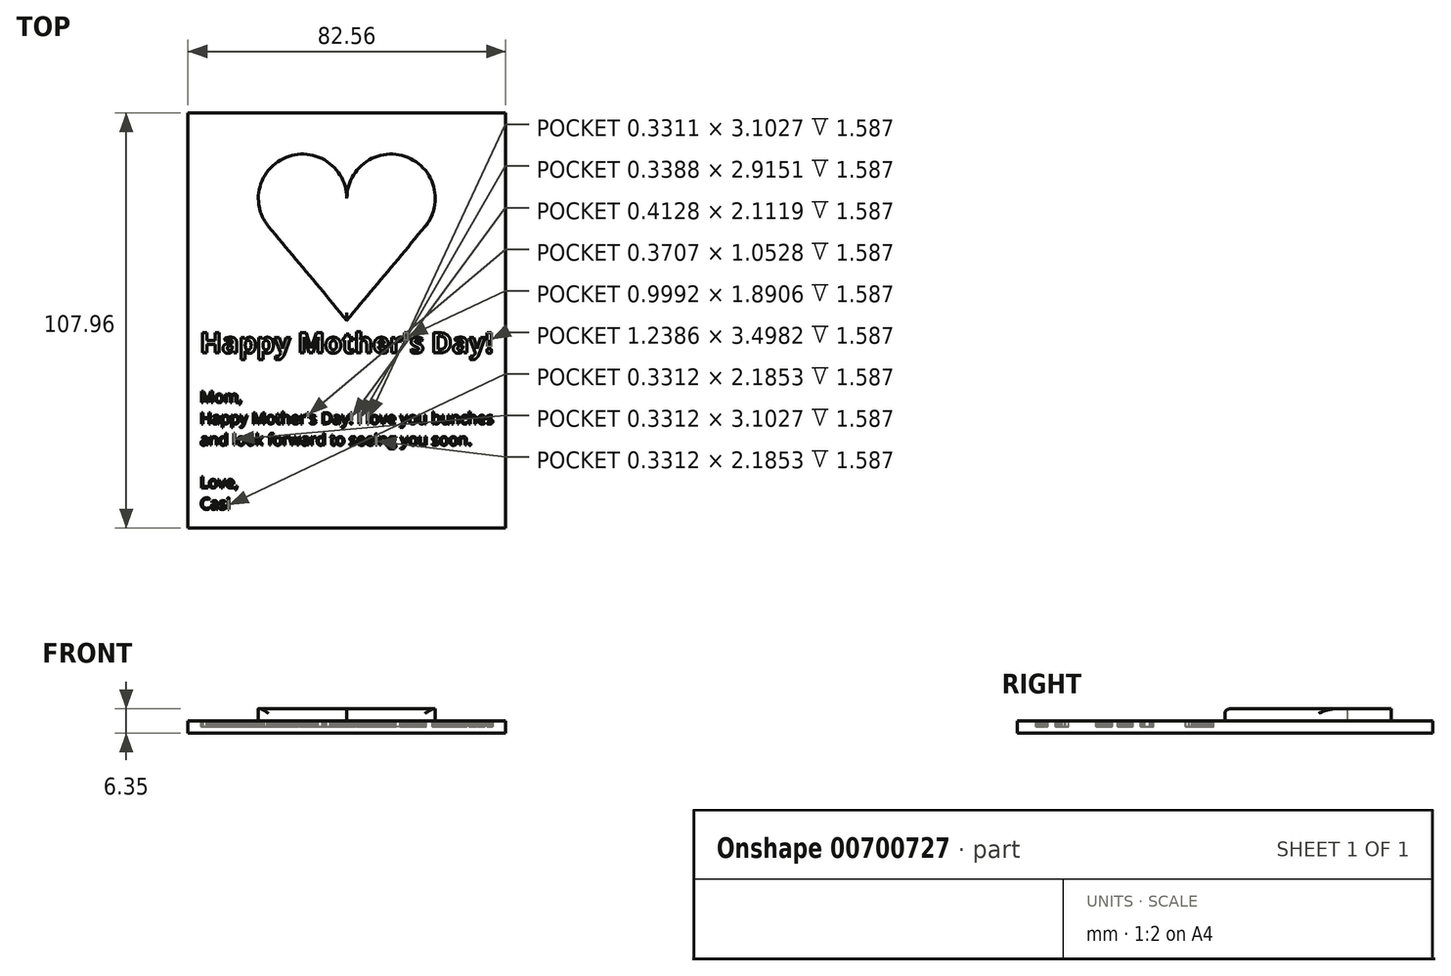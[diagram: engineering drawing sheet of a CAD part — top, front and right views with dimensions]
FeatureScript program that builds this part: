
annotation { "Feature Type Name" : "Feature", "Feature Type Description" : "" }
export const myFeature = defineFeature(function(context is Context, id is Id, definition is map)
    precondition{}
    {
        {
            var Q0;
            Q0=qCreatedBy(makeId("Top.planeOp"),FACE);
            var sketch = newSketch(context, id + "F0", { "sketchPlane" : qUnion([Q0])});
            skLineSegment(sketch, "E0.bottom", {"start": v(41.28, -53.98) * mm, "end": v(-41.28, -53.98) * mm});
            skLineSegment(sketch, "E0.top", {"start": v(41.28, 53.97) * mm, "end": v(-41.28, 53.97) * mm});
            skLineSegment(sketch, "E0.left", {"start": v(41.28, -53.98) * mm, "end": v(41.28, 53.97) * mm});
            skLineSegment(sketch, "E0.right", {"start": v(-41.28, -53.98) * mm, "end": v(-41.28, 53.97) * mm});
            skPoint(sketch, "E0.middle", {"position": v(0, 0) * mm});
            skSolve(sketch);
        }
        {
            var Q0;
            Q0 = qSketchRegion(id + "F0", true);
            extrude(context, id + "F1", {"entities" : qUnion([Q0]), "depth" : 3.17 * mm, "offsetDistance" : 25.4 * mm});
        }
        {
            var Q0;
            Q0=makeQuery(id+"F1.opExtrude","CAP_FACE",FACE,{"disambiguationData":[OSD([sQuery(id+"F0.wireOp",EDGE,"E0.bottom"),sQuery(id+"F0.wireOp",EDGE,"E0.top"),sQuery(id+"F0.wireOp",EDGE,"E0.left"),sQuery(id+"F0.wireOp",EDGE,"E0.right")])],"isStart":false});
            var sketch = newSketch(context, id + "F2", { "sketchPlane" : qUnion([Q0])});
            skLineSegment(sketch, "E1", {"start": v(0, 0) * mm, "end": v(-20.32, 24.4) * mm});
            skArc(sketch, "E2", {"start": v(-20.32, 24.4) * mm, "mid": v(-15.4, 42.55) * mm, "end": v(0, 31.75) * mm});
            skArc(sketch, "E3.MirrorCS", {"start": v(20.32, 24.4) * mm, "mid": v(15.4, 42.55) * mm, "end": v(0, 31.75) * mm});
            skLineSegment(sketch, "E4.MirrorCS", {"start": v(0, 0) * mm, "end": v(20.32, 24.4) * mm});
            skSolve(sketch);
        }
        {
            var Q0;
            Q0 = qSketchRegion(id + "F2", true);
            extrude(context, id + "F3", {"entities" : qUnion([Q0]), "operationType" : NewBodyOperationType.ADD, "depth" : 3.17 * mm, "offsetDistance" : 25.4 * mm});
        }
        {
            var Q0;
            Q0=makeQuery(id+"F1.opExtrude","CAP_FACE",FACE,{"disambiguationData":[OSD([sQuery(id+"F0.wireOp",EDGE,"E0.bottom"),sQuery(id+"F0.wireOp",EDGE,"E0.top"),sQuery(id+"F0.wireOp",EDGE,"E0.left"),sQuery(id+"F0.wireOp",EDGE,"E0.right")])],"isStart":false});
            var sketch = newSketch(context, id + "F4", { "sketchPlane" : qUnion([Q0])});
            skText(sketch, "E5", { "text": "Happy Mother\'s Day!", "fontName": "OpenSans-Bold.ttf"});
            skText(sketch, "E6", { "text": "Mom,\nHappy Mother\'s Day! I love you bunches \nand look forward to seeing you soon.\n\nLove,\nCasi", "fontName": "OpenSans-Regular.ttf"});
            const initialGuessF4  = {"E5": [-0.0381, -0.00846, 1, 0, 0.00528], "E6": [-0.0381, -0.02135, 1, 0, 0.00294]};
            skSetInitialGuess(sketch, initialGuessF4);
            skSolve(sketch);
        }
        {
            var Q0;
            Q0 = qSketchRegion(id + "F4", true);
            extrude(context, id + "F5", {"entities" : qUnion([Q0]), "operationType" : NewBodyOperationType.REMOVE, "oppositeDirection" : true, "depth" : 1.59 * mm, "offsetDistance" : 25.4 * mm});
        }
        {
            var Q0;
            Q0=makeQuery(id+"F3.opExtrude","CAP_EDGE",EDGE,{"disambiguationData":[OSD([sQuery(id+"F2.wireOp",EDGE,"E1")])],"isStart":false});
            var Q1;
            Q1=makeQuery(id+"F3.opExtrude","CAP_EDGE",EDGE,{"disambiguationData":[OSD([sQuery(id+"F2.wireOp",EDGE,"E4.MirrorCS")])],"isStart":false});
            fillet(context, id + "F6", {"entities" : qUnion([Q0, Q1]), "radius" : 1.27 * mm, "rho" : 0.5, "crossSection" : FilletCrossSection.CONIC, "allowEdgeOverflow" : false});
        }
    });
